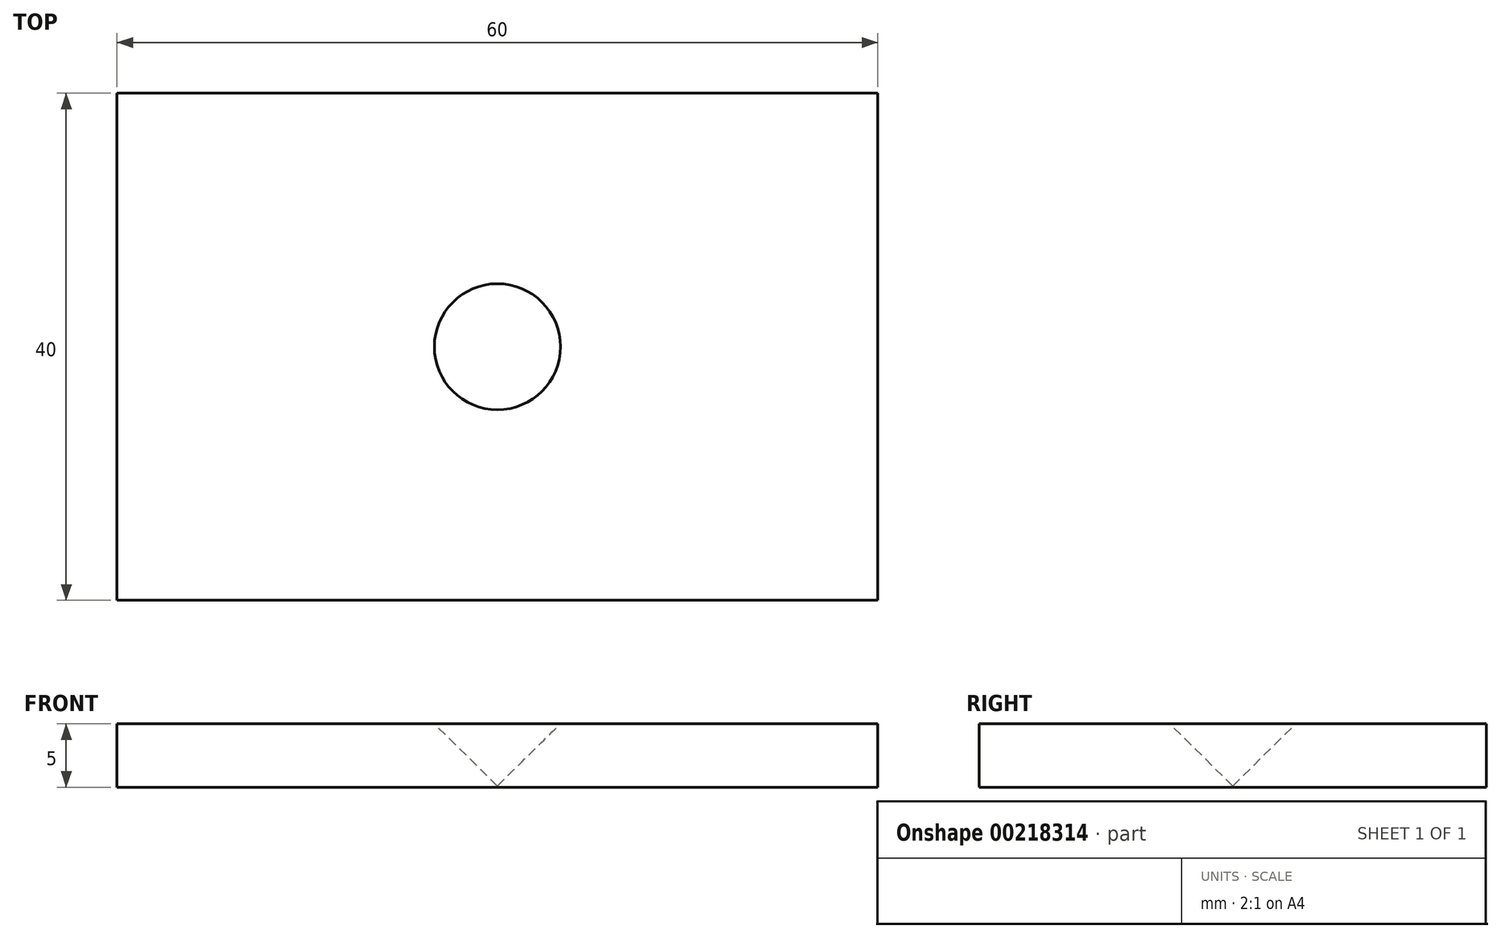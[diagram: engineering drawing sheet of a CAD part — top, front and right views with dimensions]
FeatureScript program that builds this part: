
annotation { "Feature Type Name" : "Feature", "Feature Type Description" : "" }
export const myFeature = defineFeature(function(context is Context, id is Id, definition is map)
    precondition{}
    {
        {
            var Q0;
            Q0=qCreatedBy(makeId("Top.planeOp"),FACE);
            var sketch = newSketch(context, id + "F0", { "sketchPlane" : qUnion([Q0])});
            skLineSegment(sketch, "E0.bottom", {"start": v(30, -20) * mm, "end": v(-30, -20) * mm});
            skLineSegment(sketch, "E0.top", {"start": v(30, 20) * mm, "end": v(-30, 20) * mm});
            skLineSegment(sketch, "E0.left", {"start": v(30, -20) * mm, "end": v(30, 20) * mm});
            skLineSegment(sketch, "E0.right", {"start": v(-30, -20) * mm, "end": v(-30, 20) * mm});
            skPoint(sketch, "E0.middle", {"position": v(0, 0) * mm});
            skSolve(sketch);
        }
        {
            var Q0;
            Q0 = qSketchRegion(id + "F0", true);
            extrude(context, id + "F1", {"entities" : qUnion([Q0]), "depth" : 5 * mm});
        }
        {
            var Q0;
            Q0=qCreatedBy(makeId("Front.planeOp"),FACE);
            var sketch = newSketch(context, id + "F2", { "sketchPlane" : qUnion([Q0])});
            skLineSegment(sketch, "E1", {"start": v(-7, 7) * mm, "end": v(0, 7) * mm});
            skLineSegment(sketch, "E2", {"start": v(0, -12.17) * mm, "end": v(0, 0) * mm, "construction": true});
            skPoint(sketch, "E2.endSnap0", {"position": v(0, 0) * mm});
            skLineSegment(sketch, "E3.trimOffspring", {"start": v(0, 7) * mm, "end": v(0, 30.73) * mm, "construction": true});
            skLineSegment(sketch, "E4", {"start": v(-7, 7) * mm, "end": v(0, 0.1) * mm});
            skLineSegment(sketch, "E5", {"start": v(0, 0.1) * mm, "end": v(0, 7) * mm});
            skSolve(sketch);
        }
        {
            var Q0;
            Q0=makeQuery(id+"F2.imprint","IMPRINT",FACE,{"disambiguationData":[TD([[makeQuery(id+"F2.imprint","IMPRINT",EDGE,{"derivedFrom":sQuery(id+"F2.wireOp",EDGE,"E1")}),-1.0]])]});
            var Q1;
            Q1=sQuery(id+"F2.wireOp",EDGE,"E5");
            revolve(context, id + "F3", {"operationType" : NewBodyOperationType.REMOVE, "entities" : qUnion([Q0]), "axis" : qUnion([Q1]), "revolveType" : RevolveType.FULL, "oppositeDirection" : true});
        }
    });
